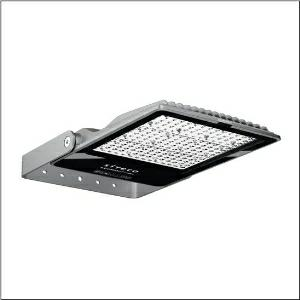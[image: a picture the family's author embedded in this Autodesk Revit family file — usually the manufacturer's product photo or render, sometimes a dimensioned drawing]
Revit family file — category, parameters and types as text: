
# Revit family: sicompact_r__31_midi___pl32_5xa7581d2k23_8dbf
name_source: partatom
category: Lighting Fixtures
units: mm (PartAtom-declared; Revit-internal decimal feet)

## family parameters
Cut with Voids When Loaded = No
Host = Face
Light Source = No
Part Type = Normal
Room Calculation Point = No
Round Connector Dimension = Use Diameter
Shared = No

## types (1)
- SiCompact® 31 midi  PL32 (1 x LED, 27000 lm, 165 W, 4000K)
    Apparent Load = 165 VA
    CIE Flux Codes = 32 69 98 100 100
    Color Rendering = 70
    Color Temperature = 4000K
    Default Elevation = 1800 mm
    Description = SiCompact® 31 midi, floodlight, primary light control with lens, of plastic, of toughened safety glass, transparent, light distribution: PL32, light emission: direct distribution, primary light characteristic: asymmetric, installation type: surface-mounted, LED, High Power LED, rated luminous flux: 27.000lm, luminous efficacy: 164lm/W, light colour: 740, colour temperature: 4000K, control gear: ON/OFF, with cable, 3x 1.5mm², mains connection: 220..240V, AC, 50/60Hz, connection cable pre-assembled, cable length: 2m, rated input power: 165W, of diecast aluminium, specular, metallic grey (RAL 9006), length: 560mm, width: 330mm, height: 62mm, bracket, of sheet steel, coated, metallic grey (RAL 9006), ON/OFF, protection rating (complete): IP66, insulation class (complete): insulation class I (protective earthing), certification: CE, ENEC, impact resistance: IK08, permissible operating ambient temperature: -40..+45°C, packaging unit: 1 piece

Light Distribution: PL32
    Height = 62 mm  [stored 0.203412 ft]
    Lamp = 1 x LED
    Lamp Light Flux = 27000 lm
    Lamp Power = 165 W
    Lamp count = 1
    Length = 560 mm
    Luminous efficacy = 164 lm/W
    Manufacturer = Siteco
    ModVariant = No
    Model = 5XA7581D2K23
    Mounting Place = Wall
    Mounting Type = Surface mounted
    Number of Poles = 1
    OnlyDefault = Yes
    Power Factor = 1
    Product Name = SiCompact® 31 midi | PL32
    Product group = floodlight | wall mounted
    ProductGroupID = 2001
    Protection Class = Protection class I
    Protection Degree = IP 66
    RLX_Detail_Level = 1
    RLX_Emergency_Light_Flux = 0 lm
    RLX_Emergency_Type = 0
    RLX_Emergency_Type_DB = No
    RlxData = <blob elided: 99241 chars, md5=2984213e>
    Socket = socket
    Standby Power = 0 W
    System Light Flux = 27000 lm
    System Power = 165 W
    Type Comments = Product without accessories
    Type Image = l_1006415.jpg
    URL = http://relux.com
    VarID = ---
    Voltage = 0 V
    Weight = 0.00 kg
    Width = 333 mm

note: [stored X ft] marks values corroborated as IEEE doubles in the binary element streams (Revit-internal decimal feet)

## geometry (parser evidence)
native form markers: Blend x4, Sweep x12
no freeform markers — native parametric forms only
